# Revit family: 01.Wichmann Kabelbox WD90 eckig_WAND
name_source: partatom
category: HLS-Bauteile
revit_build: Autodesk Revit 2018 (Build: 20170223_1515(x64)
units: mm (PartAtom-declared; Revit-internal decimal feet)

## family parameters
Basisbauteil = Wand
Beim Laden mit Abzugskörper schneiden = Nein
Bemaßung runder Anschluss = Durchmesser verwenden
Gemeinsam genutzt = Nein
Immer vertikal = Ja
Klassifizierung = Keine
OmniClass-Nummer = 23.30.20.00
OmniClass-Titel = Windows
Raumberechnungspunkt = Nein
Teiletyp = Normal

## types (68) — shared parameters
Bautiefe = 270 mm
Werkstoff = Stahl

## per-type parameters (varying)
| type | B_i | B_rohbau | Breite | HAN | H_i | H_rohbau | Höhe |
| Kabelbox WD90 eckig, 60x90x270 mm | 60 mm | 130 mm | 90 mm | 00060090 | 33 mm | 100 mm  [stored 0.328084 ft] | 60 mm |
| Kabelbox WD90 eckig, 60x120x270 mm | 90 mm | 160 mm | 120 mm | 00060120 | 33 mm | 100 mm  [stored 0.328084 ft] | 60 mm |
| Kabelbox WD90 eckig, 60x160x270 mm | 130 mm | 200 mm | 160 mm | 00060160 | 33 mm | 100 mm  [stored 0.328084 ft] | 60 mm |
| Kabelbox WD90 eckig, 60x180x270 mm | 150 mm | 220 mm | 180 mm | 00060180 | 33 mm | 100 mm  [stored 0.328084 ft] | 60 mm |
| Kabelbox WD90 eckig, 60x200x270 mm | 170 mm | 240 mm | 200 mm | 00060200 | 33 mm | 100 mm  [stored 0.328084 ft] | 60 mm |
| Kabelbox WD90 eckig, 60x240x270 mm | 210 mm | 280 mm | 240 mm | 00060240 | 33 mm | 100 mm  [stored 0.328084 ft] | 60 mm |
| Kabelbox WD90 eckig, 60x280x270 mm | 250 mm | 320 mm | 280 mm | 00060280 | 33 mm | 100 mm  [stored 0.328084 ft] | 60 mm |
| Kabelbox WD90 eckig, 60x335x270 mm | 305 mm | 375 mm | 335 mm | 00060335 | 33 mm | 100 mm  [stored 0.328084 ft] | 60 mm |
| Kabelbox WD90 eckig, 60x380x270 mm | 350 mm | 420 mm | 380 mm | 00060380 | 33 mm | 100 mm  [stored 0.328084 ft] | 60 mm |
| Kabelbox WD90 eckig, 60x435x270 mm | 405 mm | 475 mm | 435 mm | 00060435 | 33 mm | 100 mm  [stored 0.328084 ft] | 60 mm |
| Kabelbox WD90 eckig, 60x480x270 mm | 450 mm | 520 mm | 480 mm | 00060480 | 33 mm | 100 mm  [stored 0.328084 ft] | 60 mm |
| Kabelbox WD90 eckig, 60x535x270 mm | 505 mm | 575 mm | 535 mm | 00060535 | 33 mm | 100 mm  [stored 0.328084 ft] | 60 mm |
| Kabelbox WD90 eckig, 60x580x270 mm | 550 mm | 620 mm | 580 mm | 00060580 | 33 mm | 100 mm  [stored 0.328084 ft] | 60 mm |
| Kabelbox WD90 eckig, 60x640x270 mm | 610 mm | 680 mm | 640 mm | 00060640 | 33 mm | 100 mm  [stored 0.328084 ft] | 60 mm |
| Kabelbox WD90 eckig, 80x90x270 mm | 60 mm | 130 mm | 90 mm | 00080090 | 50 mm | 120 mm | 80 mm |
| Kabelbox WD90 eckig, 80x120x270 mm | 90 mm | 160 mm | 120 mm | 00080120 | 50 mm | 120 mm | 80 mm |
| Kabelbox WD90 eckig, 80x160x270 mm | 130 mm | 200 mm | 160 mm | 00080160 | 50 mm | 120 mm | 80 mm |
| Kabelbox WD90 eckig, 80x180x270 mm | 150 mm | 220 mm | 180 mm | 00080180 | 50 mm | 120 mm | 80 mm |
| Kabelbox WD90 eckig, 80x200x270 mm | 170 mm | 240 mm | 200 mm | 00080200 | 50 mm | 120 mm | 80 mm |
| Kabelbox WD90 eckig, 80x240x270 mm | 210 mm | 280 mm | 240 mm | 00080240 | 50 mm | 120 mm | 80 mm |
| Kabelbox WD90 eckig, 80x280x270 mm | 250 mm | 320 mm | 280 mm | 00080280 | 50 mm | 120 mm | 80 mm |
| Kabelbox WD90 eckig, 80x335x270 mm | 305 mm | 375 mm | 335 mm | 00080335 | 50 mm | 120 mm | 80 mm |
| Kabelbox WD90 eckig, 80x380x270 mm | 350 mm | 420 mm | 380 mm | 00080380 | 50 mm | 120 mm | 80 mm |
| Kabelbox WD90 eckig, 80x435x270 mm | 405 mm | 475 mm | 435 mm | 00080435 | 50 mm | 120 mm | 80 mm |
| Kabelbox WD90 eckig, 80x480x270 mm | 450 mm | 520 mm | 480 mm | 00080480 | 50 mm | 120 mm | 80 mm |
| Kabelbox WD90 eckig, 80x535x270 mm | 505 mm | 575 mm | 535 mm | 00080535 | 50 mm | 120 mm | 80 mm |
| Kabelbox WD90 eckig, 80x580x270 mm | 550 mm | 620 mm | 580 mm | 00080580 | 50 mm | 120 mm | 80 mm |
| Kabelbox WD90 eckig, 80x640x270 mm | 610 mm | 680 mm | 640 mm | 00080640 | 50 mm | 120 mm | 80 mm |
| Kabelbox WD90 eckig, 90x90x270 mm | 60 mm | 130 mm | 90 mm | 00090090 | 56 mm | 130 mm | 90 mm |
| Kabelbox WD90 eckig, 90x120x270 mm | 90 mm | 160 mm | 120 mm | 00090120 | 56 mm | 130 mm | 90 mm |
| Kabelbox WD90 eckig, 90x160x270 mm | 130 mm | 200 mm | 160 mm | 00090160 | 56 mm | 130 mm | 90 mm |
| Kabelbox WD90 eckig, 90x180x270 mm | 150 mm | 220 mm | 180 mm | 00090180 | 56 mm | 130 mm | 90 mm |
| Kabelbox WD90 eckig, 90x200x270 mm | 170 mm | 240 mm | 200 mm | 00090200 | 56 mm | 130 mm | 90 mm |
| Kabelbox WD90 eckig, 90x240x270 mm | 210 mm | 280 mm | 240 mm | 00090240 | 56 mm | 130 mm | 90 mm |
| Kabelbox WD90 eckig, 90x280x270 mm | 250 mm | 320 mm | 280 mm | 00090280 | 56 mm | 130 mm | 90 mm |
| Kabelbox WD90 eckig, 90x335x270 mm | 305 mm | 375 mm | 335 mm | 00090335 | 56 mm | 130 mm | 90 mm |
| Kabelbox WD90 eckig, 90x380x270 mm | 350 mm | 420 mm | 380 mm | 00090380 | 56 mm | 130 mm | 90 mm |
| Kabelbox WD90 eckig, 90x435x270 mm | 405 mm | 475 mm | 435 mm | 00090435 | 56 mm | 130 mm | 90 mm |
| Kabelbox WD90 eckig, 90x480x270 mm | 450 mm | 520 mm | 480 mm | 00090480 | 56 mm | 130 mm | 90 mm |
| Kabelbox WD90 eckig, 90x535x270 mm | 505 mm | 575 mm | 535 mm | 00090535 | 56 mm | 130 mm | 90 mm |
| Kabelbox WD90 eckig, 90x580x270 mm | 550 mm | 620 mm | 580 mm | 00090580 | 56 mm | 130 mm | 90 mm |
| Kabelbox WD90 eckig, 90x640x270 mm | 610 mm | 680 mm | 640 mm | 00090640 | 56 mm | 130 mm | 90 mm |
| Kabelbox WD90 eckig, 100x120x270 mm | 90 mm | 160 mm | 120 mm | 00100120 | 64 mm | 140 mm | 100 mm  [stored 0.328084 ft] |
| Kabelbox WD90 eckig, 100x160x270 mm | 130 mm | 200 mm | 160 mm | 00100160 | 64 mm | 140 mm | 100 mm  [stored 0.328084 ft] |
| Kabelbox WD90 eckig, 100x180x270 mm | 150 mm | 220 mm | 180 mm | 00100180 | 64 mm | 140 mm | 100 mm  [stored 0.328084 ft] |
| Kabelbox WD90 eckig, 100x200x270 mm | 170 mm | 240 mm | 200 mm | 00100200 | 64 mm | 140 mm | 100 mm  [stored 0.328084 ft] |
| Kabelbox WD90 eckig, 100x240x270 mm | 210 mm | 280 mm | 240 mm | 00100240 | 64 mm | 140 mm | 100 mm  [stored 0.328084 ft] |
| Kabelbox WD90 eckig, 100x280x270 mm | 250 mm | 320 mm | 280 mm | 00100280 | 64 mm | 140 mm | 100 mm  [stored 0.328084 ft] |
| Kabelbox WD90 eckig, 100x335x270 mm | 305 mm | 375 mm | 335 mm | 00100335 | 64 mm | 140 mm | 100 mm  [stored 0.328084 ft] |
| Kabelbox WD90 eckig, 100x380x270 mm | 350 mm | 420 mm | 380 mm | 00100380 | 64 mm | 140 mm | 100 mm  [stored 0.328084 ft] |
| Kabelbox WD90 eckig, 100x435x270 mm | 405 mm | 475 mm | 435 mm | 00100435 | 64 mm | 140 mm | 100 mm  [stored 0.328084 ft] |
| Kabelbox WD90 eckig, 100x480x270 mm | 450 mm | 520 mm | 480 mm | 00100480 | 64 mm | 140 mm | 100 mm  [stored 0.328084 ft] |
| Kabelbox WD90 eckig, 100x535x270 mm | 505 mm | 575 mm | 535 mm | 00100535 | 64 mm | 140 mm | 100 mm  [stored 0.328084 ft] |
| Kabelbox WD90 eckig, 100x580x270 mm | 550 mm | 620 mm | 580 mm | 00100580 | 64 mm | 140 mm | 100 mm  [stored 0.328084 ft] |
| Kabelbox WD90 eckig, 100x640x270 mm | 610 mm | 680 mm | 640 mm | 00100640 | 64 mm | 140 mm | 100 mm  [stored 0.328084 ft] |
| Kabelbox WD90 eckig, 110x120x270 mm | 90 mm | 160 mm | 120 mm | 00110120 | 70 mm | 150 mm | 110 mm |
| Kabelbox WD90 eckig, 110x160x270 mm | 130 mm | 200 mm | 160 mm | 00110160 | 70 mm | 150 mm | 110 mm |
| Kabelbox WD90 eckig, 110x180x270 mm | 150 mm | 220 mm | 180 mm | 00110180 | 70 mm | 150 mm | 110 mm |
| Kabelbox WD90 eckig, 110x200x270 mm | 170 mm | 240 mm | 200 mm | 00110200 | 70 mm | 150 mm | 110 mm |
| Kabelbox WD90 eckig, 110x240x270 mm | 210 mm | 280 mm | 240 mm | 00110240 | 70 mm | 150 mm | 110 mm |
| Kabelbox WD90 eckig, 110x280x270 mm | 250 mm | 320 mm | 280 mm | 00110280 | 70 mm | 150 mm | 110 mm |
| Kabelbox WD90 eckig, 110x335x270 mm | 305 mm | 375 mm | 335 mm | 00110335 | 70 mm | 150 mm | 110 mm |
| Kabelbox WD90 eckig, 110x380x270 mm | 350 mm | 420 mm | 380 mm | 00110380 | 70 mm | 150 mm | 110 mm |
| Kabelbox WD90 eckig, 110x435x270 mm | 405 mm | 475 mm | 435 mm | 00110435 | 70 mm | 150 mm | 110 mm |
| Kabelbox WD90 eckig, 110x480x270 mm | 450 mm | 520 mm | 480 mm | 00110480 | 70 mm | 150 mm | 110 mm |
| Kabelbox WD90 eckig, 110x535x270 mm | 505 mm | 575 mm | 535 mm | 00110535 | 70 mm | 150 mm | 110 mm |
| Kabelbox WD90 eckig, 110x580x270 mm | 550 mm | 620 mm | 580 mm | 00110580 | 70 mm | 150 mm | 110 mm |
| Kabelbox WD90 eckig, 110x640x270 mm | 610 mm | 680 mm | 640 mm | 00110640 | 70 mm | 150 mm | 110 mm |

note: [stored X ft] marks values corroborated as IEEE doubles in the binary element streams (Revit-internal decimal feet)

## geometry (parser evidence)
native form markers: Sweep x5
no freeform markers — native parametric forms only
